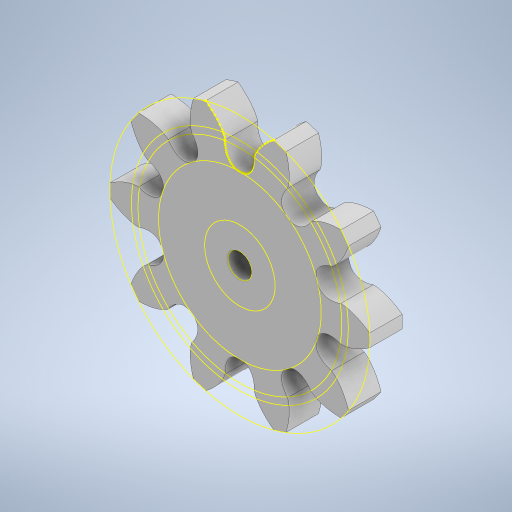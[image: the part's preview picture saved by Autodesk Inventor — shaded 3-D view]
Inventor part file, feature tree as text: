
AUTODESK INVENTOR PART (.ipt)
format: ipt  version: 2023 (Build 270158000, 158)  size: 429,568 bytes
history: native  units: mm
features: other x3, sketch x2, extrude x1, projected_geometry x1
ambient origin geometry x8: Origin, YZ Plane, XZ Plane, XY Plane, X Axis, Y Axis, Z Axis, Center Point
bodies: Solid1 (feature_tree)
feature tree (7):
  other  "pinion_V6"
  extrude  "Extrusion1"  Depth=10.0mm TaperAngle=0.0deg
  other  "Solid1::pinion_V6"
  other  "TaggingFeature1"
  sketch  "Sketch1"  dims[d0=10.0mm d1=10.0mm d2=0.0mm]
  sketch  "Sketch2"
  projected_geometry  "Projected Loop1"
